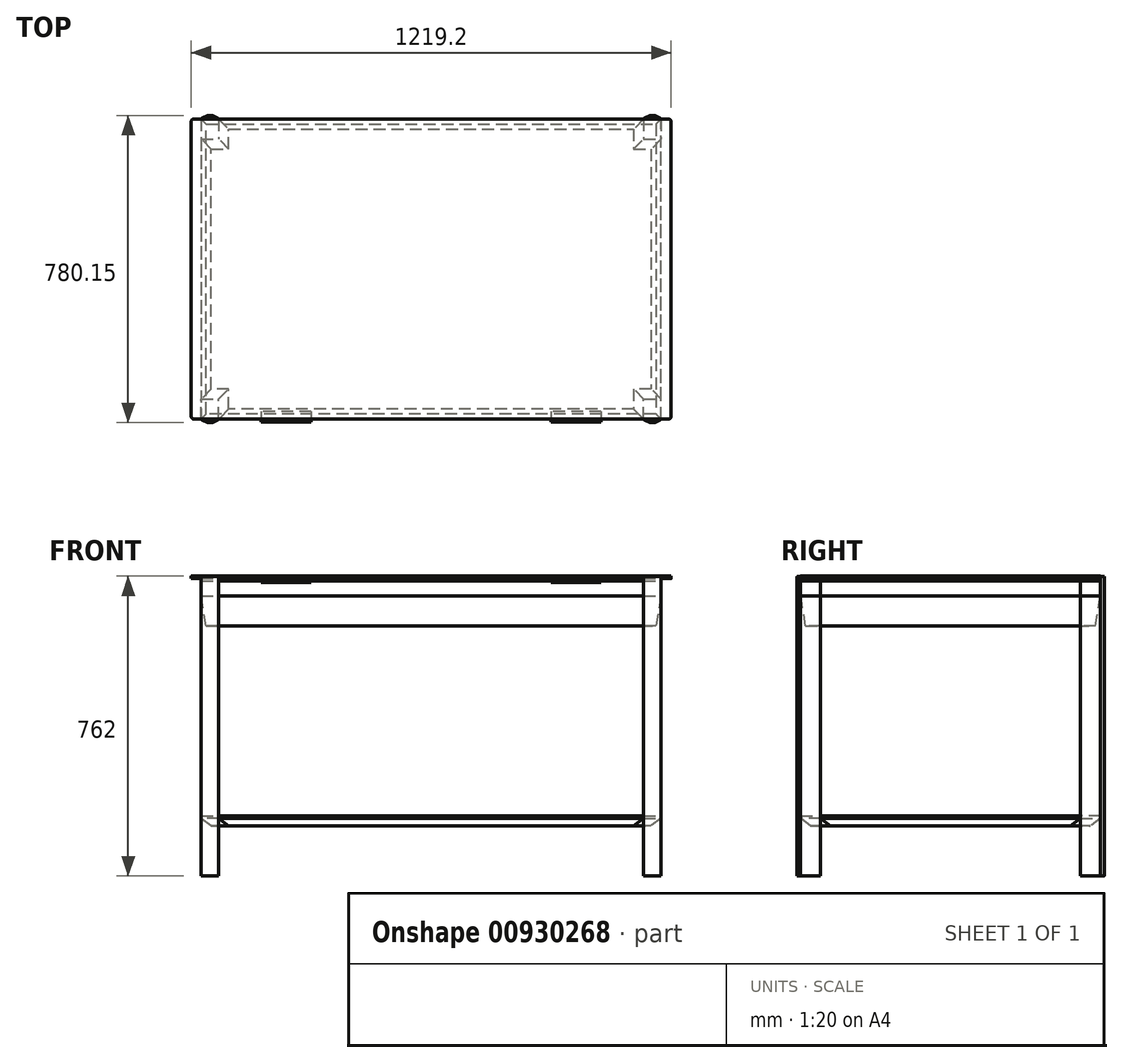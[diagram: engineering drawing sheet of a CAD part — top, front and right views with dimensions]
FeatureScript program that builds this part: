
annotation { "Feature Type Name" : "Feature", "Feature Type Description" : "" }
export const myFeature = defineFeature(function(context is Context, id is Id, definition is map)
    precondition{}
    {
        {
            var Q0;
            Q0=qCreatedBy(makeId("Top.planeOp"),FACE);
            var sketch = newSketch(context, id + "F0", { "sketchPlane" : qUnion([Q0])});
            skLineSegment(sketch, "E0.bottom", {"start": v(-1117.6, 694.48) * mm, "end": v(88.9, 694.48) * mm});
            skLineSegment(sketch, "E0.top", {"start": v(-1117.6, -67.52) * mm, "end": v(88.9, -67.52) * mm});
            skLineSegment(sketch, "E0.left", {"start": v(-1123.95, 688.13) * mm, "end": v(-1123.95, -61.17) * mm});
            skLineSegment(sketch, "E0.right", {"start": v(95.25, 688.13) * mm, "end": v(95.25, -61.17) * mm});
            skLineSegment(sketch, "E1.bottom", {"start": v(-1098.55, 694.48) * mm, "end": v(-1054.1, 694.48) * mm});
            skLineSegment(sketch, "E1.top", {"start": v(-1098.55, 643.68) * mm, "end": v(-1054.1, 643.68) * mm});
            skLineSegment(sketch, "E1.left", {"start": v(-1098.55, 694.48) * mm, "end": v(-1098.55, 643.68) * mm});
            skLineSegment(sketch, "E1.right", {"start": v(-1054.1, 694.48) * mm, "end": v(-1054.1, 643.68) * mm});
            skLineSegment(sketch, "E2.bottom", {"start": v(-1098.55, -67.52) * mm, "end": v(-1054.1, -67.52) * mm});
            skLineSegment(sketch, "E2.top", {"start": v(-1098.55, -16.72) * mm, "end": v(-1054.1, -16.72) * mm});
            skLineSegment(sketch, "E2.left", {"start": v(-1098.55, -67.52) * mm, "end": v(-1098.55, -16.72) * mm});
            skLineSegment(sketch, "E2.right", {"start": v(-1054.1, -67.52) * mm, "end": v(-1054.1, -16.72) * mm});
            skLineSegment(sketch, "E3.bottom", {"start": v(25.4, 694.48) * mm, "end": v(69.85, 694.48) * mm});
            skLineSegment(sketch, "E3.top", {"start": v(25.4, 643.68) * mm, "end": v(69.85, 643.68) * mm});
            skLineSegment(sketch, "E3.left", {"start": v(25.4, 694.48) * mm, "end": v(25.4, 643.68) * mm});
            skLineSegment(sketch, "E3.right", {"start": v(69.85, 694.48) * mm, "end": v(69.85, 643.68) * mm});
            skLineSegment(sketch, "E4.bottom", {"start": v(25.4, -67.52) * mm, "end": v(69.85, -67.52) * mm});
            skLineSegment(sketch, "E4.top", {"start": v(25.4, -16.72) * mm, "end": v(69.85, -16.72) * mm});
            skLineSegment(sketch, "E4.left", {"start": v(25.4, -67.52) * mm, "end": v(25.4, -16.72) * mm});
            skLineSegment(sketch, "E4.right", {"start": v(69.85, -67.52) * mm, "end": v(69.85, -16.72) * mm});
            skPoint(sketch, "E5", {"position": v(-1076.33, 694.48) * mm});
            skArc(sketch, "E6", {"start": v(-1054.1, 694.48) * mm, "mid": v(-1076.33, 703.55) * mm, "end": v(-1098.55, 694.48) * mm});
            skArc(sketch, "E7", {"start": v(69.85, 694.48) * mm, "mid": v(47.62, 703.55) * mm, "end": v(25.4, 694.48) * mm});
            skArc(sketch, "E8", {"start": v(-1098.55, -67.52) * mm, "mid": v(-1076.33, -76.6) * mm, "end": v(-1054.1, -67.52) * mm});
            skArc(sketch, "E9", {"start": v(25.4, -67.52) * mm, "mid": v(47.62, -76.6) * mm, "end": v(69.85, -67.52) * mm});
            skLineSegment(sketch, "E10", {"start": v(-1098.55, -16.72) * mm, "end": v(-1098.55, 643.68) * mm});
            skLineSegment(sketch, "E11", {"start": v(69.85, 643.68) * mm, "end": v(69.85, -16.72) * mm});
            skPoint(sketch, "E12.visualSharp", {"position": v(-1123.95, 694.48) * mm});
            skArc(sketch, "E12.filletArc", {"start": v(-1117.6, 694.48) * mm, "mid": v(-1122.1, 692.62) * mm, "end": v(-1123.95, 688.13) * mm});
            skPoint(sketch, "E13.visualSharp", {"position": v(-1123.95, -67.52) * mm});
            skArc(sketch, "E13.filletArc", {"start": v(-1123.95, -61.17) * mm, "mid": v(-1122.1, -65.66) * mm, "end": v(-1117.6, -67.52) * mm});
            skPoint(sketch, "E14.visualSharp", {"position": v(95.25, -67.52) * mm});
            skArc(sketch, "E14.filletArc", {"start": v(88.9, -67.52) * mm, "mid": v(93.4, -65.66) * mm, "end": v(95.25, -61.17) * mm});
            skPoint(sketch, "E15.visualSharp", {"position": v(95.25, 694.48) * mm});
            skArc(sketch, "E15.filletArc", {"start": v(95.25, 688.13) * mm, "mid": v(93.4, 692.62) * mm, "end": v(88.9, 694.48) * mm});
            skSolve(sketch);
        }
        {
            var Q0;
            Q0=makeQuery(id+"F0.imprint","IMPRINT",FACE,{"disambiguationData":[TD([[makeQuery(id+"F0.imprint","IMPRINT",EDGE,{"derivedFrom":sQuery(id+"F0.wireOp",EDGE,"E2.top")}),-1.0]])]});
            var Q1;
            Q1=makeQuery(id+"F0.imprint","IMPRINT",FACE,{"disambiguationData":[TD([[makeQuery(id+"F0.imprint","IMPRINT",EDGE,{"derivedFrom":sQuery(id+"F0.wireOp",EDGE,"E2.top")}),-1.0]])]});
            var Q2;
            Q2=makeQuery(id+"F0.imprint","IMPRINT",FACE,{"disambiguationData":[TD([[makeQuery(id+"F0.imprint","IMPRINT",EDGE,{"derivedFrom":sQuery(id+"F0.wireOp",EDGE,"E0.left")}),1.0]])]});
            var Q3;
            Q3=makeQuery(id+"F0.imprint","IMPRINT",FACE,{"disambiguationData":[TD([[makeQuery(id+"F0.imprint","IMPRINT",EDGE,{"derivedFrom":sQuery(id+"F0.wireOp",EDGE,"E1.top")}),1.0]])]});
            var Q4;
            Q4=makeQuery(id+"F0.imprint","IMPRINT",FACE,{"disambiguationData":[TD([[makeQuery(id+"F0.imprint","IMPRINT",EDGE,{"derivedFrom":sQuery(id+"F0.wireOp",EDGE,"E1.top")}),1.0]])]});
            var Q5;
            Q5=makeQuery(id+"F0.imprint","IMPRINT",FACE,{"disambiguationData":[TD([[makeQuery(id+"F0.imprint","IMPRINT",EDGE,{"derivedFrom":sQuery(id+"F0.wireOp",EDGE,"E3.top")}),1.0]])]});
            var Q6;
            Q6=makeQuery(id+"F0.imprint","IMPRINT",FACE,{"disambiguationData":[TD([[makeQuery(id+"F0.imprint","IMPRINT",EDGE,{"derivedFrom":sQuery(id+"F0.wireOp",EDGE,"E3.top")}),1.0]])]});
            var Q7;
            Q7=makeQuery(id+"F0.imprint","IMPRINT",FACE,{"disambiguationData":[TD([[makeQuery(id+"F0.imprint","IMPRINT",EDGE,{"derivedFrom":sQuery(id+"F0.wireOp",EDGE,"E4.top")}),-1.0]])]});
            var Q8;
            Q8=makeQuery(id+"F0.imprint","IMPRINT",FACE,{"disambiguationData":[TD([[makeQuery(id+"F0.imprint","IMPRINT",EDGE,{"derivedFrom":sQuery(id+"F0.wireOp",EDGE,"E4.top")}),-1.0]])]});
            var Q9;
            Q9=makeQuery(id+"F0.imprint","IMPRINT",FACE,{"disambiguationData":[TD([[makeQuery(id+"F0.imprint","IMPRINT",EDGE,{"derivedFrom":sQuery(id+"F0.wireOp",EDGE,"E1.top")}),-1.0]])]});
            var Q10;
            Q10=makeQuery(id+"F0.imprint","IMPRINT",FACE,{"disambiguationData":[TD([[makeQuery(id+"F0.imprint","IMPRINT",EDGE,{"derivedFrom":sQuery(id+"F0.wireOp",EDGE,"E0.right")}),-1.0]])]});
            extrude(context, id + "F1", {"entities" : qUnion([Q0, Q1, Q2, Q3, Q4, Q5, Q6, Q7, Q8, Q9, Q10]), "oppositeDirection" : true, "depth" : 6.35 * mm, "offsetDistance" : 25.4 * mm});
        }
        {
            var Q0;
            {var subQ0=sQuery(id+"F0.wireOp",EDGE,"E8");Q0=makeQuery(id+"F0.imprint","IMPRINT",FACE,{"disambiguationData":[TD([[makeQuery(id+"F0.imprint","IMPRINT",EDGE,{"derivedFrom":subQ0}),1.0]])]});}
            var Q1;
            {var subQ0=sQuery(id+"F0.wireOp",EDGE,"E6");Q1=makeQuery(id+"F0.imprint","IMPRINT",FACE,{"disambiguationData":[TD([[makeQuery(id+"F0.imprint","IMPRINT",EDGE,{"derivedFrom":subQ0}),1.0]])]});}
            var Q2;
            Q2=makeQuery(id+"F0.imprint","IMPRINT",FACE,{"disambiguationData":[TD([[makeQuery(id+"F0.imprint","IMPRINT",EDGE,{"derivedFrom":sQuery(id+"F0.wireOp",EDGE,"E1.top")}),1.0]])]});
            var Q3;
            Q3=makeQuery(id+"F0.imprint","IMPRINT",FACE,{"disambiguationData":[TD([[makeQuery(id+"F0.imprint","IMPRINT",EDGE,{"derivedFrom":sQuery(id+"F0.wireOp",EDGE,"E1.top")}),1.0]])]});
            var Q4;
            Q4=makeQuery(id+"F0.imprint","IMPRINT",FACE,{"disambiguationData":[TD([[makeQuery(id+"F0.imprint","IMPRINT",EDGE,{"derivedFrom":sQuery(id+"F0.wireOp",EDGE,"E2.top")}),-1.0]])]});
            var Q5;
            Q5=makeQuery(id+"F0.imprint","IMPRINT",FACE,{"disambiguationData":[TD([[makeQuery(id+"F0.imprint","IMPRINT",EDGE,{"derivedFrom":sQuery(id+"F0.wireOp",EDGE,"E2.top")}),-1.0]])]});
            var Q6;
            Q6=makeQuery(id+"F0.imprint","IMPRINT",FACE,{"disambiguationData":[TD([[makeQuery(id+"F0.imprint","IMPRINT",EDGE,{"derivedFrom":sQuery(id+"F0.wireOp",EDGE,"E4.top")}),-1.0]])]});
            var Q7;
            Q7=makeQuery(id+"F0.imprint","IMPRINT",FACE,{"disambiguationData":[TD([[makeQuery(id+"F0.imprint","IMPRINT",EDGE,{"derivedFrom":sQuery(id+"F0.wireOp",EDGE,"E4.top")}),-1.0]])]});
            var Q8;
            {var subQ0=sQuery(id+"F0.wireOp",EDGE,"E9");Q8=makeQuery(id+"F0.imprint","IMPRINT",FACE,{"disambiguationData":[TD([[makeQuery(id+"F0.imprint","IMPRINT",EDGE,{"derivedFrom":subQ0}),1.0]])]});}
            var Q9;
            Q9=makeQuery(id+"F0.imprint","IMPRINT",FACE,{"disambiguationData":[TD([[makeQuery(id+"F0.imprint","IMPRINT",EDGE,{"derivedFrom":sQuery(id+"F0.wireOp",EDGE,"E3.top")}),1.0]])]});
            var Q10;
            {var subQ0=sQuery(id+"F0.wireOp",EDGE,"E7");Q10=makeQuery(id+"F0.imprint","IMPRINT",FACE,{"disambiguationData":[TD([[makeQuery(id+"F0.imprint","IMPRINT",EDGE,{"derivedFrom":subQ0}),1.0]])]});}
            var Q11;
            Q11=makeQuery(id+"F0.imprint","IMPRINT",FACE,{"disambiguationData":[TD([[makeQuery(id+"F0.imprint","IMPRINT",EDGE,{"derivedFrom":sQuery(id+"F0.wireOp",EDGE,"E3.top")}),1.0]])]});
            extrude(context, id + "F2", {"entities" : qUnion([Q0, Q1, Q2, Q3, Q4, Q5, Q6, Q7, Q8, Q9, Q10, Q11]), "oppositeDirection" : true, "depth" : 762 * mm, "offsetDistance" : 25.4 * mm, "hasSecondDirection" : true, "secondDirectionOppositeDirection" : true, "secondDirectionDepth" : 1.59 * mm});
        }
        {
            var Q0;
            Q0=makeQuery(id+"F0.imprint","IMPRINT",FACE,{"disambiguationData":[TD([[makeQuery(id+"F0.imprint","IMPRINT",EDGE,{"derivedFrom":sQuery(id+"F0.wireOp",EDGE,"E1.top")}),-1.0]])]});
            var Q1;
            Q1=makeQuery(id+"F0.imprint","IMPRINT",FACE,{"disambiguationData":[TD([[makeQuery(id+"F0.imprint","IMPRINT",EDGE,{"derivedFrom":sQuery(id+"F0.wireOp",EDGE,"E2.top")}),-1.0]])]});
            var Q2;
            Q2=makeQuery(id+"F0.imprint","IMPRINT",FACE,{"disambiguationData":[TD([[makeQuery(id+"F0.imprint","IMPRINT",EDGE,{"derivedFrom":sQuery(id+"F0.wireOp",EDGE,"E1.top")}),1.0]])]});
            var Q3;
            Q3=makeQuery(id+"F0.imprint","IMPRINT",FACE,{"disambiguationData":[TD([[makeQuery(id+"F0.imprint","IMPRINT",EDGE,{"derivedFrom":sQuery(id+"F0.wireOp",EDGE,"E3.top")}),1.0]])]});
            var Q4;
            Q4=makeQuery(id+"F0.imprint","IMPRINT",FACE,{"disambiguationData":[TD([[makeQuery(id+"F0.imprint","IMPRINT",EDGE,{"derivedFrom":sQuery(id+"F0.wireOp",EDGE,"E4.top")}),-1.0]])]});
            extrude(context, id + "F3", {"entities" : qUnion([Q0, Q1, Q2, Q3, Q4]), "oppositeDirection" : true, "depth" : 127 * mm, "offsetDistance" : 25.4 * mm, "hasSecondDirection" : true, "secondDirectionOppositeDirection" : true, "secondDirectionDepth" : 12.7 * mm});
        }
        {
            var Q0;
            Q0=makeQuery(id+"F2.opExtrude","SWEPT_FACE",FACE,{"disambiguationData":[OSD([sQuery(id+"F0.wireOp",EDGE,"E2.left")])]});
            var sketch = newSketch(context, id + "F4", { "sketchPlane" : qUnion([Q0])});
            skLineSegment(sketch, "E16.bottom", {"start": v(48.47, -12.7) * mm, "end": v(73.87, -12.7) * mm});
            skLineSegment(sketch, "E16.top", {"start": v(48.47, -14.38) * mm, "end": v(73.87, -14.38) * mm});
            skLineSegment(sketch, "E16.left", {"start": v(48.47, -12.7) * mm, "end": v(48.47, -14.38) * mm});
            skLineSegment(sketch, "E16.right", {"start": v(73.87, -12.7) * mm, "end": v(73.87, -14.38) * mm});
            skArc(sketch, "E17", {"start": v(73.87, -12.7) * mm, "mid": v(75.06, -15.56) * mm, "end": v(72.2, -14.38) * mm});
            skSolve(sketch);
        }
        {
            var Q0;
            {var subQ0=sQuery(id+"F4.wireOp",EDGE,"E16.right");Q0=makeQuery(id+"F4.imprint","IMPRINT",FACE,{"disambiguationData":[TD([[makeQuery(id+"F4.imprint","IMPRINT",EDGE,{"derivedFrom":subQ0}),1.0]])]});}
            var Q1;
            {var subQ0=sQuery(id+"F4.wireOp",EDGE,"E16.right");Q1=makeQuery(id+"F4.imprint","IMPRINT",FACE,{"disambiguationData":[TD([[makeQuery(id+"F4.imprint","IMPRINT",EDGE,{"derivedFrom":subQ0}),-1.0]])]});}
            var Q2;
            {var subQ0=sQuery(id+"F4.wireOp",EDGE,"E16.left");Q2=makeQuery(id+"F4.imprint","IMPRINT",FACE,{"disambiguationData":[TD([[makeQuery(id+"F4.imprint","IMPRINT",EDGE,{"derivedFrom":subQ0}),1.0]])]});}
            extrude(context, id + "F5", {"entities" : qUnion([Q0, Q1, Q2]), "oppositeDirection" : true, "depth" : 279.4 * mm, "offsetDistance" : 25.4 * mm, "hasSecondDirection" : true, "secondDirectionOppositeDirection" : true, "secondDirectionDepth" : 152.4 * mm});
        }
        {
            var Q0;
            {var subQ0=sQuery(id+"F4.wireOp",EDGE,"E16.left");Q0=makeQuery(id+"F4.imprint","IMPRINT",FACE,{"disambiguationData":[TD([[makeQuery(id+"F4.imprint","IMPRINT",EDGE,{"derivedFrom":subQ0}),1.0]])]});}
            var Q1;
            {var subQ0=sQuery(id+"F4.wireOp",EDGE,"E16.right");Q1=makeQuery(id+"F4.imprint","IMPRINT",FACE,{"disambiguationData":[TD([[makeQuery(id+"F4.imprint","IMPRINT",EDGE,{"derivedFrom":subQ0}),-1.0]])]});}
            var Q2;
            {var subQ0=sQuery(id+"F4.wireOp",EDGE,"E16.right");Q2=makeQuery(id+"F4.imprint","IMPRINT",FACE,{"disambiguationData":[TD([[makeQuery(id+"F4.imprint","IMPRINT",EDGE,{"derivedFrom":subQ0}),1.0]])]});}
            extrude(context, id + "F6", {"entities" : qUnion([Q0, Q1, Q2]), "oppositeDirection" : true, "depth" : 1016 * mm, "offsetDistance" : 25.4 * mm, "hasSecondDirection" : true, "secondDirectionOppositeDirection" : true, "secondDirectionDepth" : 889 * mm});
        }
        {
            var Q0;
            Q0=makeQuery(id+"F3.opExtrude","CAP_FACE",FACE,{"disambiguationData":[OSD([sQuery(id+"F0.wireOp",EDGE,"E0.bottom"),sQuery(id+"F0.wireOp",EDGE,"E0.top"),sQuery(id+"F0.wireOp",EDGE,"E1.left"),sQuery(id+"F0.wireOp",EDGE,"E2.left"),sQuery(id+"F0.wireOp",EDGE,"E3.right"),sQuery(id+"F0.wireOp",EDGE,"E4.right"),sQuery(id+"F0.wireOp",EDGE,"E10"),sQuery(id+"F0.wireOp",EDGE,"E11")])],"isStart":false});
            chamfer(context, id + "F7", {"entities" : qUnion([Q0]), "chamferType" : ChamferType.TWO_OFFSETS, "width1" : 76.2 * mm, "oppositeDirection" : true, "width2" : 12.7 * mm, "tangentPropagation" : true});
        }
        {
            var Q0;
            Q0=makeQuery(id+"F0.imprint","IMPRINT",FACE,{"disambiguationData":[TD([[makeQuery(id+"F0.imprint","IMPRINT",EDGE,{"derivedFrom":sQuery(id+"F0.wireOp",EDGE,"E1.top")}),-1.0]])]});
            extrude(context, id + "F8", {"entities" : qUnion([Q0]), "oppositeDirection" : true, "depth" : 635 * mm, "offsetDistance" : 25.4 * mm, "hasSecondDirection" : true, "secondDirectionOppositeDirection" : true, "secondDirectionDepth" : 609.6 * mm});
        }
        {
            var Q0;
            Q0=makeQuery(id+"F8.opExtrude","CAP_FACE",FACE,{"disambiguationData":[OSD([sQuery(id+"F0.wireOp",EDGE,"E0.bottom"),sQuery(id+"F0.wireOp",EDGE,"E0.top"),sQuery(id+"F0.wireOp",EDGE,"E1.top"),sQuery(id+"F0.wireOp",EDGE,"E1.right"),sQuery(id+"F0.wireOp",EDGE,"E2.top"),sQuery(id+"F0.wireOp",EDGE,"E2.right"),sQuery(id+"F0.wireOp",EDGE,"E3.top"),sQuery(id+"F0.wireOp",EDGE,"E3.left"),sQuery(id+"F0.wireOp",EDGE,"E4.top"),sQuery(id+"F0.wireOp",EDGE,"E4.left"),sQuery(id+"F0.wireOp",EDGE,"E10"),sQuery(id+"F0.wireOp",EDGE,"E11")])],"isStart":false});
            chamfer(context, id + "F9", {"entities" : qUnion([Q0]), "chamferType" : ChamferType.TWO_OFFSETS, "width1" : 25.4 * mm, "oppositeDirection" : false, "width2" : 19.05 * mm, "tangentPropagation" : true});
        }
    });
